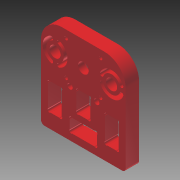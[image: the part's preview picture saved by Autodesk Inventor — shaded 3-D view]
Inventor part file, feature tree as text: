
AUTODESK INVENTOR PART (.ipt)
format: ipt  version: 2012 SP1 (Build 160190100, 190)  size: 278,016 bytes
history: native  units: in
note: dims shown in document units (in); Inventor stores cm internally (conversion verified against a paired STEP export)
features: other x6, extrude x4
ambient origin geometry x8: Origin, YZ Plane, XZ Plane, XY Plane, X Axis, Y Axis, Z Axis, Center Point
bodies: Solid1 (feature_tree)
feature tree (10):
  other  "skeleton.ipt"
  other  "DRILL-THROUGH"
  other  "POCKET_1-4"
  other  "POCKET_1-8"
  other  "STOCK_12MM"
  extrude  "Extrusion1"  Depth=0.3937in
  extrude  "Extrusion2"  Depth=0.4724in
  extrude  "Extrusion3"  TaperAngle=0.0deg  [1 undecoded]
  extrude  "Extrusion4"  Depth=0.125in TaperAngle=0.0deg
  other  "THROUGH-CUT"
note: 1 required parameter value undecoded (feature->parameter linkage not recoverable at this tier; creation-order binding heuristic only, values carry confidence <= 0.55)
